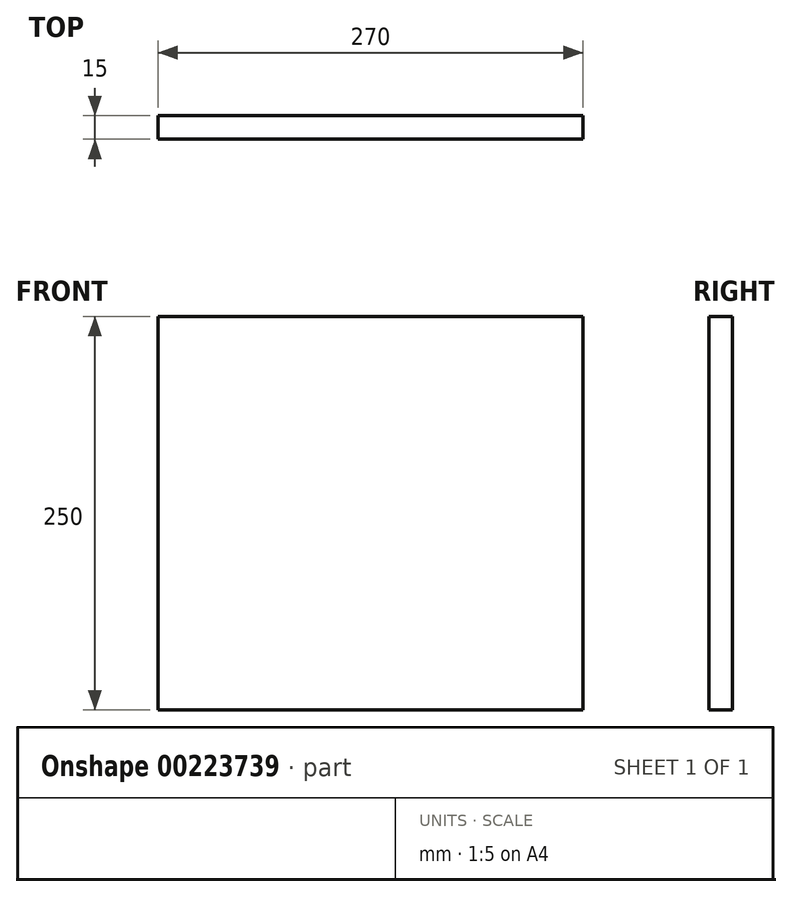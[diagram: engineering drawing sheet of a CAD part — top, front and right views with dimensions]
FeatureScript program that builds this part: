
annotation { "Feature Type Name" : "Feature", "Feature Type Description" : "" }
export const myFeature = defineFeature(function(context is Context, id is Id, definition is map)
    precondition{}
    {
        {
            var Q0;
            Q0=qCreatedBy(makeId("Front.planeOp"),FACE);
            var sketch = newSketch(context, id + "F0", { "sketchPlane" : qUnion([Q0])});
            skLineSegment(sketch, "E0.bottom", {"start": v(135, -125) * mm, "end": v(-135, -125) * mm});
            skLineSegment(sketch, "E0.top", {"start": v(135, 125) * mm, "end": v(-135, 125) * mm});
            skLineSegment(sketch, "E0.left", {"start": v(135, -125) * mm, "end": v(135, 125) * mm});
            skLineSegment(sketch, "E0.right", {"start": v(-135, -125) * mm, "end": v(-135, 125) * mm});
            skPoint(sketch, "E0.middle", {"position": v(0, 0) * mm});
            skSolve(sketch);
        }
        {
            var Q0;
            Q0=qSketchRegion(id+"F0",true);
            extrude(context, id + "F1", {"entities" : qUnion([Q0]), "depth" : 15 * mm});
        }
    });
